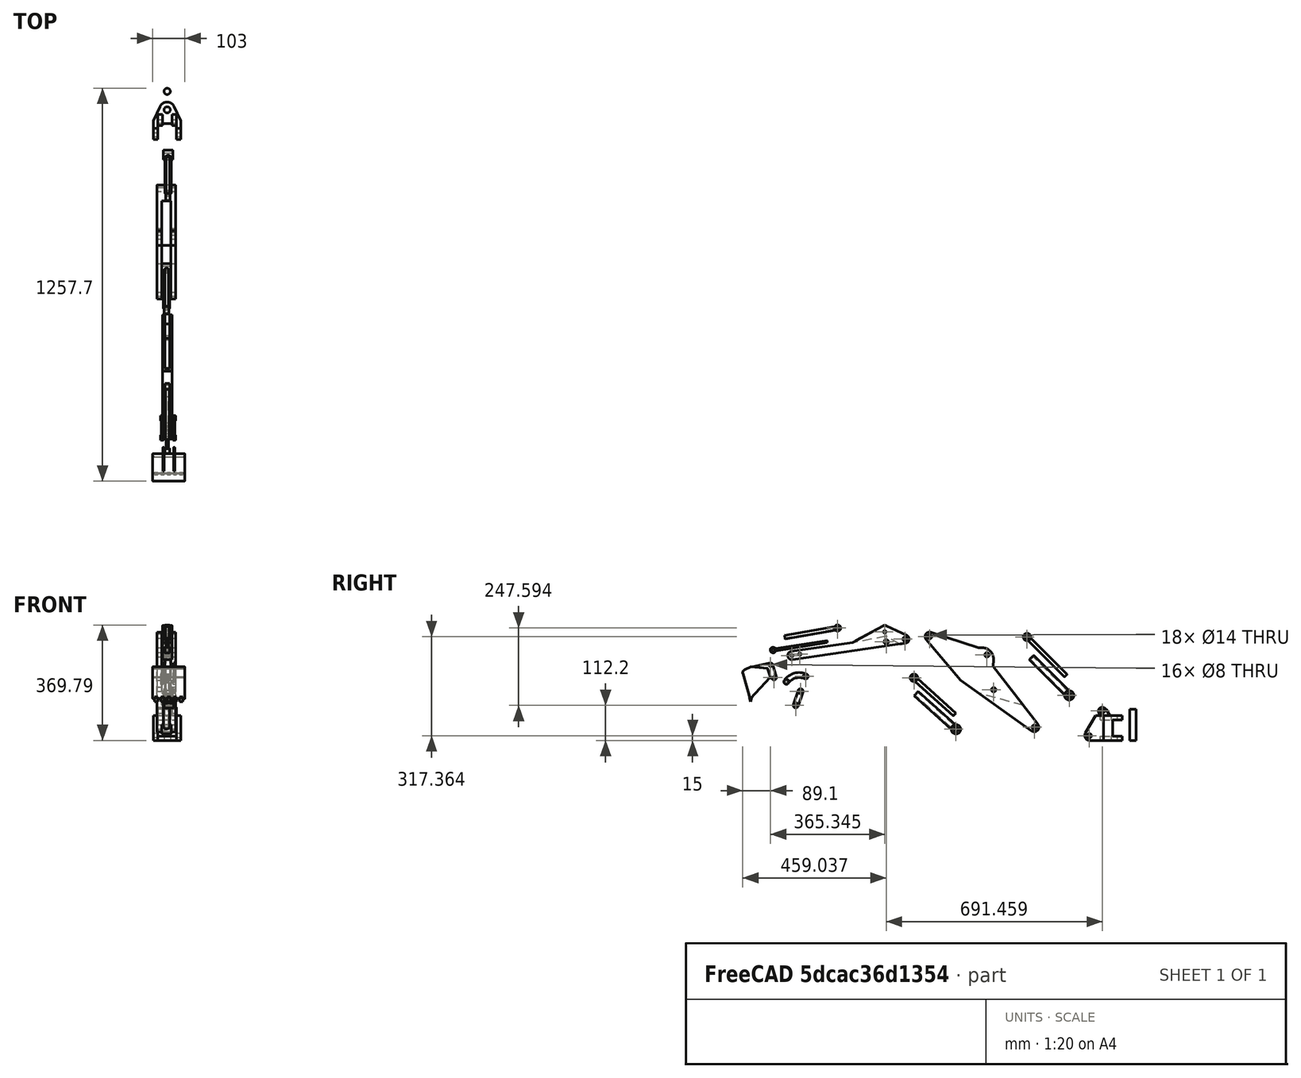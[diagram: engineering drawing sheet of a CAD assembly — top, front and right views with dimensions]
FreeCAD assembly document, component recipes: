
FREECAD ASSEMBLY — COMPONENT RECIPES ("brazo-hidraulico")

This assembly document has 13 components, labeled P0..P12 below (a component is one placed body or linked part). 0 of them carry a construction recipe — the FreeCAD feature program that regenerates the part from scratch, quoted from this document or its linked companion documents; the rest are supplied as boundary geometry only. No exploded tour is included for this assembly.
COMPONENT P0 — geometry summary ("Base001"; no construction recipe available for this part):
  bounding box: 119.7 x 106.0 x 88.3 mm
  tessellated surface: 4,364 triangles
  volume: 241281 mm^3 (22% of its bounding box)
  symmetry: mirror-symmetric across its x mid-plane
COMPONENT P1 — geometry summary ("BasePin001"; no construction recipe available for this part):
  bounding box: 100.0 x 20.0 x 20.0 mm
  tessellated surface: 500 triangles
  volume: 31416 mm^3 (79% of its bounding box)
  symmetry: 2-fold rotationally symmetric about the x axis; 2-fold rotationally symmetric about the y axis; revolution-symmetric about the z axis through its bounding-box center; mirror-symmetric across its x mid-plane, y mid-plane, z mid-plane
COMPONENT P2 — geometry summary ("Boom001"; no construction recipe available for this part):
  bounding box: 436.3 x 203.7 x 60.9 mm
  tessellated surface: 4,520 triangles
  volume: 1204575 mm^3 (22% of its bounding box)
  symmetry: mirror-symmetric across its x mid-plane
COMPONENT P3 — geometry summary ("BoomCylinderInner001"; no construction recipe available for this part):
  bounding box: 177.3 x 82.0 x 15.1 mm
  tessellated surface: 1,472 triangles
  volume: 22989 mm^3 (10% of its bounding box)
  symmetry: mirror-symmetric across its x mid-plane
COMPONENT P4 — geometry summary ("BoomCylinderOuter001"; no construction recipe available for this part):
  bounding box: 177.7 x 87.1 x 30.1 mm
  tessellated surface: 1,966 triangles
  volume: 48197 mm^3 (10% of its bounding box)
  symmetry: mirror-symmetric across its x mid-plane
COMPONENT P5 — geometry summary ("Bucket001"; no construction recipe available for this part):
  bounding box: 117.6 x 103.4 x 100.6 mm
  tessellated surface: 3,994 triangles
  volume: 58312 mm^3 (5% of its bounding box)
  symmetry: mirror-symmetric across its x mid-plane
COMPONENT P6 — geometry summary ("BucketCylinderInner001"; no construction recipe available for this part):
  bounding box: 173.2 x 77.1 x 15.1 mm
  tessellated surface: 1,172 triangles
  volume: 9046 mm^3 (4% of its bounding box)
COMPONENT P7 — geometry summary ("BucketCylinderOuter001"; no construction recipe available for this part):
  bounding box: 171.1 x 78.8 x 15.1 mm
  tessellated surface: 1,556 triangles
  volume: 16012 mm^3 (8% of its bounding box)
COMPONENT P8 — geometry summary ("BucketLink004"; no construction recipe available for this part):
  bounding box: 62.9 x 30.3 x 26.8 mm
  tessellated surface: 3,660 triangles
  volume: 12304 mm^3 (24% of its bounding box)
  symmetry: mirror-symmetric across its x mid-plane
COMPONENT P9 — geometry summary ("BucketLink003"; no construction recipe available for this part):
  bounding box: 73.0 x 48.2 x 47.1 mm
  tessellated surface: 4,319 triangles
  volume: 17079 mm^3 (10% of its bounding box)
COMPONENT P10 — geometry summary ("Stick001"; no construction recipe available for this part):
  bounding box: 379.8 x 121.2 x 31.8 mm
  tessellated surface: 3,756 triangles
  volume: 333942 mm^3 (23% of its bounding box)
  symmetry: mirror-symmetric across its x mid-plane
COMPONENT P11 — geometry summary ("StickCylinderInner001"; no construction recipe available for this part):
  bounding box: 184.3 x 56.4 x 15.1 mm
  tessellated surface: 1,472 triangles
  volume: 22989 mm^3 (15% of its bounding box)
  symmetry: mirror-symmetric across its x mid-plane
COMPONENT P12 — geometry summary ("StickCylinderOuter001"; no construction recipe available for this part):
  bounding box: 184.0 x 62.4 x 30.1 mm
  tessellated surface: 1,966 triangles
  volume: 48197 mm^3 (14% of its bounding box)
  symmetry: mirror-symmetric across its x mid-plane
PROVENANCE & LICENSES
A FreeCAD (.FCStd) document from a public repository crawl; recipes are the document's own serialized feature recipes (and, for linked parts, companion documents' recipes).
License: as declared in the source repository (recorded in the dataset sidecar).
